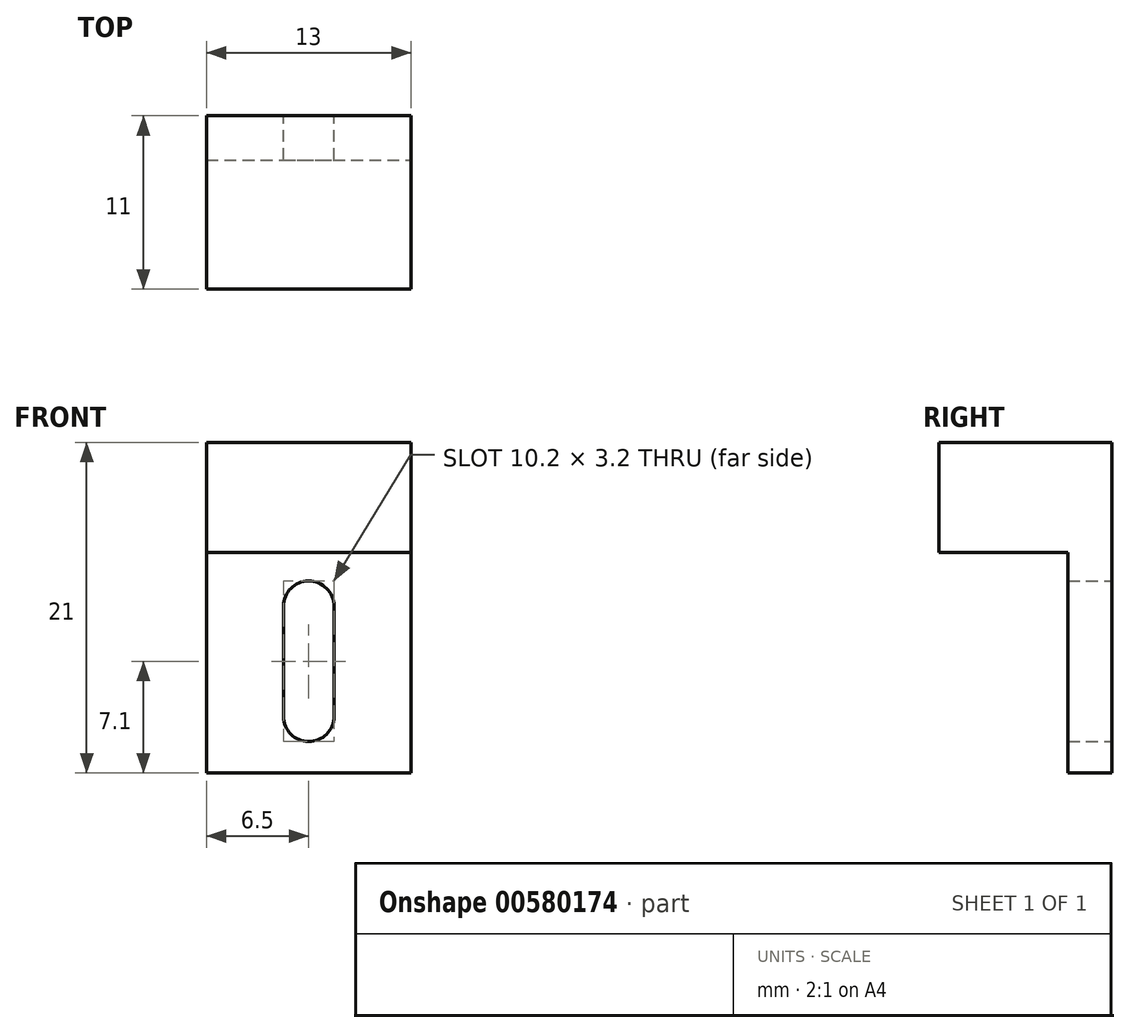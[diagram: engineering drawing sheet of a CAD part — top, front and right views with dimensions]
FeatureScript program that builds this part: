
annotation { "Feature Type Name" : "Feature", "Feature Type Description" : "" }
export const myFeature = defineFeature(function(context is Context, id is Id, definition is map)
    precondition{}
    {
        {
            var Q0;
            Q0=qCreatedBy(makeId("Front.planeOp"),FACE);
            var sketch = newSketch(context, id + "F0", { "sketchPlane" : qUnion([Q0])});
            skLineSegment(sketch, "E0.bottom", {"start": v(-6.5, 0) * mm, "end": v(6.5, 0) * mm});
            skLineSegment(sketch, "E0.top", {"start": v(-6.5, 21) * mm, "end": v(6.5, 21) * mm});
            skLineSegment(sketch, "E0.left", {"start": v(-6.5, 0) * mm, "end": v(-6.5, 21) * mm});
            skLineSegment(sketch, "E0.right", {"start": v(6.5, 0) * mm, "end": v(6.5, 21) * mm});
            skArc(sketch, "E1", {"start": v(-1.6, 3.6) * mm, "mid": v(0, 2) * mm, "end": v(1.6, 3.6) * mm});
            skArc(sketch, "E2", {"start": v(1.6, 10.6) * mm, "mid": v(0, 12.2) * mm, "end": v(-1.6, 10.6) * mm});
            skLineSegment(sketch, "E3", {"start": v(-1.6, 3.6) * mm, "end": v(-1.6, 10.6) * mm});
            skLineSegment(sketch, "E4", {"start": v(1.6, 10.6) * mm, "end": v(1.6, 3.6) * mm});
            skSolve(sketch);
        }
        {
            var Q0;
            Q0=makeQuery(id+"F0.imprint","IMPRINT",FACE,{"disambiguationData":[TD([[makeQuery(id+"F0.imprint","IMPRINT",EDGE,{"derivedFrom":sQuery(id+"F0.wireOp",EDGE,"E0.bottom")}),1.0]])]});
            extrude(context, id + "F1", {"entities" : qUnion([Q0]), "depth" : 11 * mm, "offsetDistance" : 25 * mm});
        }
        {
            var Q0;
            Q0=makeQuery(id+"F1.opExtrude","CAP_FACE",FACE,{"disambiguationData":[OSD([sQuery(id+"F0.wireOp",EDGE,"E0.bottom"),sQuery(id+"F0.wireOp",EDGE,"E0.top"),sQuery(id+"F0.wireOp",EDGE,"E0.left"),sQuery(id+"F0.wireOp",EDGE,"E0.right"),sQuery(id+"F0.wireOp",EDGE,"E1"),sQuery(id+"F0.wireOp",EDGE,"E2"),sQuery(id+"F0.wireOp",EDGE,"E3"),sQuery(id+"F0.wireOp",EDGE,"E4")])],"isStart":false});
            var sketch = newSketch(context, id + "F2", { "sketchPlane" : qUnion([Q0])});
            skLineSegment(sketch, "E5.bottom", {"start": v(-6.5, 0) * mm, "end": v(6.5, 0) * mm});
            skLineSegment(sketch, "E5.top", {"start": v(-6.5, 14) * mm, "end": v(6.5, 14) * mm});
            skLineSegment(sketch, "E5.left", {"start": v(-6.5, 0) * mm, "end": v(-6.5, 14) * mm});
            skLineSegment(sketch, "E5.right", {"start": v(6.5, 0) * mm, "end": v(6.5, 14) * mm});
            skSolve(sketch);
        }
        {
            var Q0;
            Q0=makeQuery(id+"F2.imprint","IMPRINT",FACE,{"disambiguationData":[TD([[makeQuery(id+"F2.imprint","IMPRINT",EDGE,{"derivedFrom":sQuery(id+"F2.wireOp",EDGE,"E5.bottom")}),1.0]])]});
            extrude(context, id + "F3", {"entities" : qUnion([Q0]), "operationType" : NewBodyOperationType.REMOVE, "oppositeDirection" : true, "depth" : 8.2 * mm, "offsetDistance" : 25 * mm});
        }
    });
